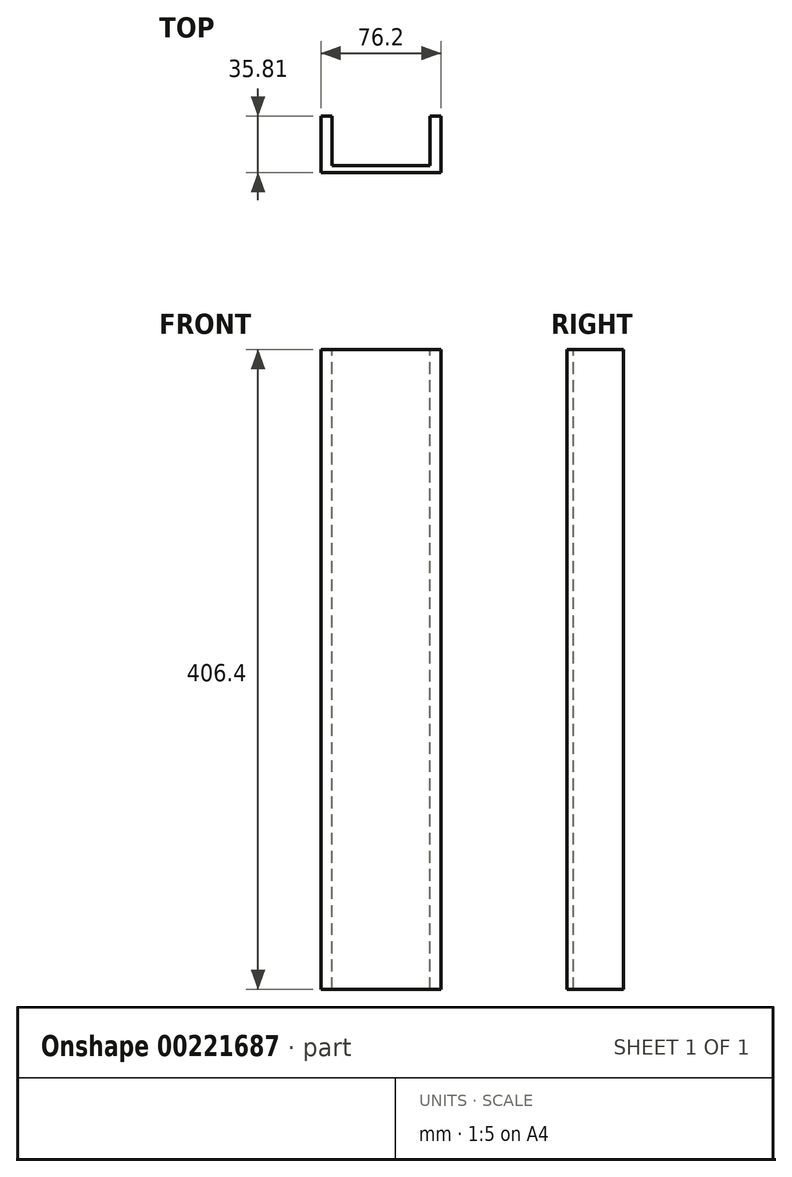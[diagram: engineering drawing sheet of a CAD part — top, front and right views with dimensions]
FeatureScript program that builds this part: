
annotation { "Feature Type Name" : "Feature", "Feature Type Description" : "" }
export const myFeature = defineFeature(function(context is Context, id is Id, definition is map)
    precondition{}
    {
        {
            var Q0;
            Q0=qCreatedBy(makeId("Front.planeOp"),FACE);
            var sketch = newSketch(context, id + "F0", { "sketchPlane" : qUnion([Q0])});
            skLineSegment(sketch, "E0.bottom", {"start": v(-35.22, -333.52) * mm, "end": v(40.98, -333.52) * mm});
            skLineSegment(sketch, "E0.top", {"start": v(-35.22, 72.88) * mm, "end": v(40.98, 72.88) * mm});
            skLineSegment(sketch, "E0.left", {"start": v(-35.22, -333.52) * mm, "end": v(-35.22, 72.88) * mm});
            skLineSegment(sketch, "E0.right", {"start": v(40.98, -333.52) * mm, "end": v(40.98, 72.88) * mm});
            skSolve(sketch);
        }
        {
            var Q0;
            Q0 = qSketchRegion(id + "F0", true);
            extrude(context, id + "F1", {"entities" : qUnion([Q0]), "oppositeDirection" : true, "depth" : 35.81 * mm});
        }
        {
            var Q0;
            Q0=makeQuery(id+"F1.opExtrude","SWEPT_FACE",FACE,{"disambiguationData":[OSD([sQuery(id+"F0.wireOp",EDGE,"E0.top")])]});
            var sketch = newSketch(context, id + "F2", { "sketchPlane" : qUnion([Q0])});
            skLineSegment(sketch, "E1.bottom", {"start": v(-28.3, 35.81) * mm, "end": v(34.04, 35.81) * mm});
            skLineSegment(sketch, "E1.top", {"start": v(-28.3, 4.32) * mm, "end": v(34.04, 4.32) * mm});
            skLineSegment(sketch, "E1.left", {"start": v(-28.3, 35.81) * mm, "end": v(-28.3, 4.32) * mm});
            skLineSegment(sketch, "E1.right", {"start": v(34.04, 35.81) * mm, "end": v(34.04, 4.32) * mm});
            skSolve(sketch);
        }
        {
            var Q0;
            Q0 = qSketchRegion(id + "F2", true);
            extrude(context, id + "F3", {"entities" : qUnion([Q0]), "operationType" : NewBodyOperationType.REMOVE, "endBound" : BoundingType.THROUGH_ALL, "oppositeDirection" : true, "depth" : 25.4 * mm});
        }
    });
